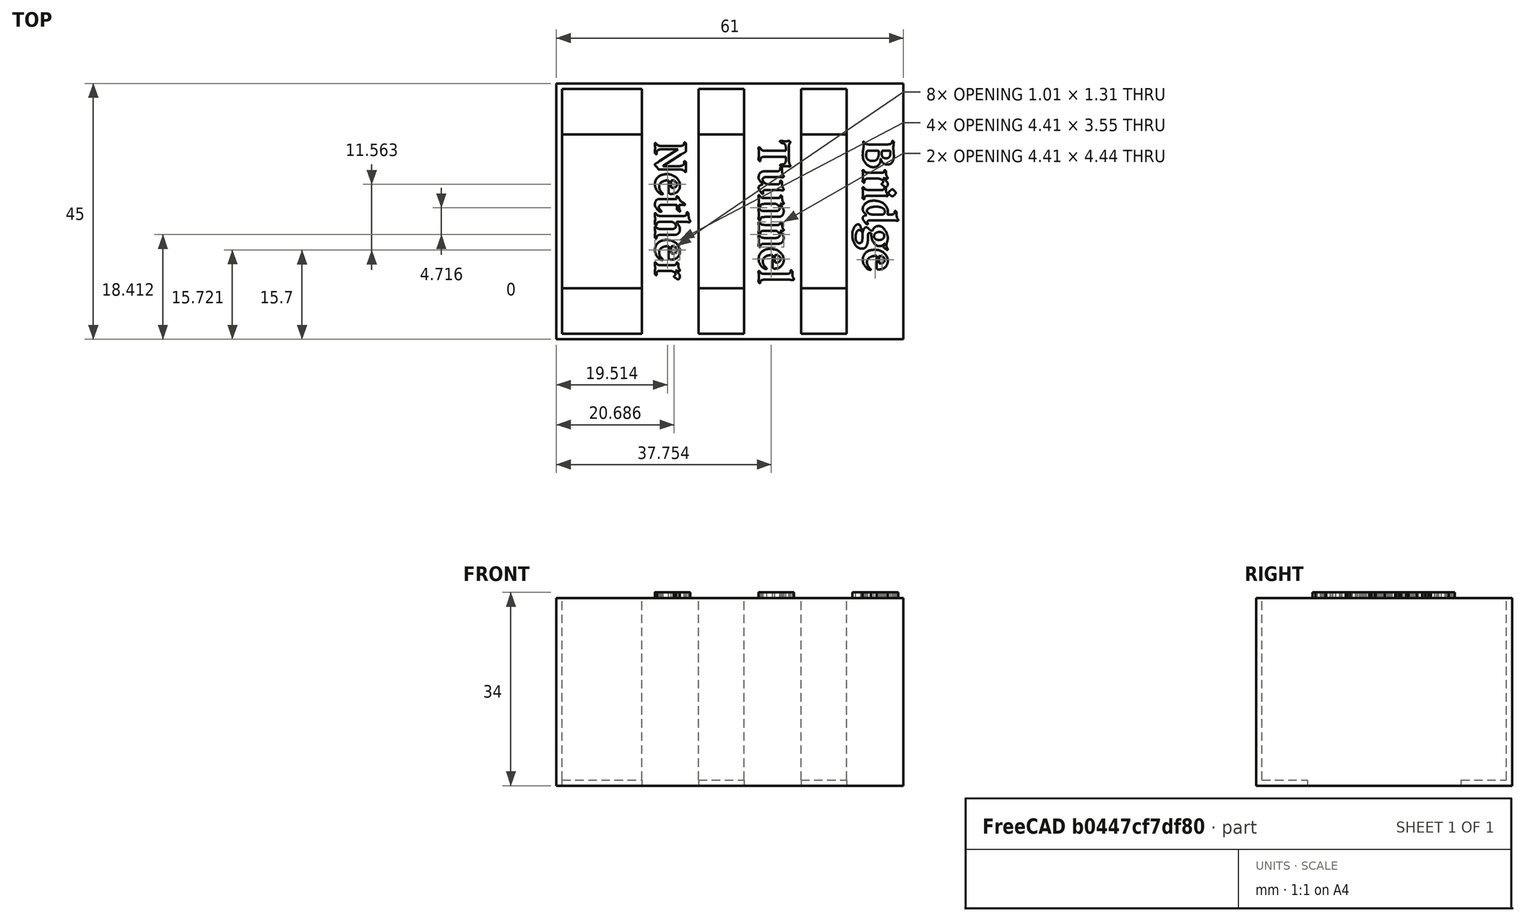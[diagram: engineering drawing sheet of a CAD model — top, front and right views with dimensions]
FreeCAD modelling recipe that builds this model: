
FCSTD DOCUMENT  (FreeCAD 0.18R4 (GitTag))
Label: lost_realms
License: All rights reserved
LicenseURL: http://en.wikipedia.org/wiki/All_rights_reserved
objects: Part::FeaturePython×21, Part::Box×9, Part::MultiFuse×7, Part::Extrusion×5, Part::Part2DObjectPython×3, Part::Cut×2, Part::Feature×1, Part::Plane×1, App::DocumentObjectGroup×1
note: 49 computed .brp shape members not serialized (recipe doc carries the construction recipe); baked Part::Feature solids carry a one-line shape summary decoded from their .brp

FEATURE [Part::Box] Box  label="Cube"
  AttacherType = Attacher::AttachEngine3D
  Height = 33
  Length = 202
  Placement = pos=(0,-1,0) rot=(0,0,1;0rad)
  Width = 45
FEATURE [Part::Box] Box001  label="Cube001"
  AttacherType = Attacher::AttachEngine3D
  Height = 33
  Length = 200
  Placement = pos=(1,0,0) rot=(0,0,1;0rad)
  Width = 43
FEATURE [Part::Cut] Cut
  Base = -> Box
  Tool = -> Box001
FEATURE [Part::Box] Box002  label="Cube002"
  AttacherType = Attacher::AttachEngine3D
  Height = 1
  Length = 202
  Width = 8
FEATURE [Part::Box] Box003  label="Cube003"
  AttacherType = Attacher::AttachEngine3D
  Height = 1
  Length = 202
  Placement = pos=(0,35,0) rot=(0,0,1;0rad)
  Width = 8
FEATURE [Part::MultiFuse] Fusion
  Shapes = -> [Cut,Box002,Box003]
FEATURE [Part::Box] Box004  label="Cube004"
  AttacherType = Attacher::AttachEngine3D
  Height = 33
  Length = 10
  Placement = pos=(15,0,0) rot=(0,0,1;0rad)
  Width = 43
FEATURE [Part::Box] Box005  label="Cube005"
  AttacherType = Attacher::AttachEngine3D
  Height = 33
  Length = 10
  Placement = pos=(33,0,0) rot=(0,0,1;0rad)
  Width = 43
FEATURE [Part::Box] Box006  label="Cube006"
  AttacherType = Attacher::AttachEngine3D
  Height = 33
  Length = 10
  Placement = pos=(51,0,0) rot=(0,0,1;0rad)
  Width = 43
FEATURE [Part::Box] Box007  label="Cube007"
  AttacherType = Attacher::AttachEngine3D
  Height = 33
  Length = 150
  Placement = pos=(61,-1,0) rot=(0,0,1;0rad)
  Width = 45
FEATURE [Part::MultiFuse] Fusion001
  Shapes = -> [Fusion,Box005,Box004,Box006]
FEATURE [Part::Cut] Cut001
  Base = -> Fusion001
  Tool = -> Box007
FEATURE [Part::Box] Box008  label="Cube008"
  AttacherType = Attacher::AttachEngine3D
  Height = 33
  Length = 10
  Placement = pos=(51,0,0) rot=(0,0,1;0rad)
  Width = 43
FEATURE [Part::MultiFuse] Fusion002
  Shapes = -> [Cut001,Box008]
FEATURE [Part::Part2DObjectPython] ShapeString  # Draft 2D object (typed FeaturePython)
  FontFile = <userpath>/Downloads/talisman/Caxton Bold.otf
  Size = 3
  String = Bridge
  Tracking = 0
FEATURE [Part::Extrusion] Extrude
  Base = -> ShapeString
  Dir = (0,0,1)
  DirMode = 2
  FaceMakerClass = Part::FaceMakerBullseye
  LengthFwd = 1
  LengthRev = 0
  Solid = false
  Symmetric = false
FEATURE [Part::Extrusion] Extrude001
  Base = -> ShapeString
  Dir = (0,0,1)
  DirMode = 2
  FaceMakerClass = Part::FaceMakerBullseye
  LengthFwd = 1
  LengthRev = 0
  Solid = false
  Symmetric = false
FEATURE [Part::Part2DObjectPython] ShapeString001  # Draft 2D object (typed FeaturePython)
  FontFile = <userpath>/Downloads/talisman/Caxton Bold.otf
  Placement = pos=(33,40.7,33) rot=(0,0,1;0rad)
  Size = 3
  String = Tunnel
  Tracking = 0
FEATURE [Part::Extrusion] Extrude002
  Base = -> ShapeString001
  Dir = (0,0,1)
  DirMode = 2
  FaceMakerClass = Part::FaceMakerBullseye
  LengthFwd = 1
  LengthRev = 0
  Placement = pos=(-5,67,0) rot=(0,0,-1;1.5708rad)
  Solid = false
  Symmetric = false
FEATURE [Part::Part2DObjectPython] ShapeString002  # Draft 2D object (typed FeaturePython)
  FontFile = <userpath>/Downloads/talisman/Caxton Bold.otf
  Placement = pos=(16.76,32.46,33) rot=(0,0,1;0rad)
  Size = 3
  String = Nether
  Tracking = 0
FEATURE [Part::Extrusion] Extrude003
  Base = -> ShapeString002
  Dir = (0,0,1)
  DirMode = 2
  FaceMakerClass = Part::FaceMakerBullseye
  LengthFwd = 1
  LengthRev = 0
  Solid = false
  Symmetric = false
FEATURE [Part::Extrusion] Extrude004
  Base = -> ShapeString002
  Dir = (0,0,1)
  DirMode = 2
  FaceMakerClass = Part::FaceMakerBullseye
  LengthFwd = 1
  LengthRev = 0
  Solid = false
  Symmetric = false
FEATURE [Part::MultiFuse] Fusion004
  Placement = pos=(-15,50.5,0) rot=(0,0,-1;1.5708rad)
  Shapes = -> [Extrude003,Extrude004]
FEATURE [Part::MultiFuse] Fusion006
  Placement = pos=(54,34,33) rot=(0,0,-1;1.5708rad)
  Shapes = -> [Extrude001,Extrude]
FEATURE [Part::MultiFuse] Fusion007
  Shapes = -> [Fusion006,Fusion002,Fusion004,Extrude002]
FEATURE [Part::Feature] Fusion007001  label="Fusion008"
  shape: bbox 61 x 45 x 34 mm, 504 faces (baked)
FEATURE [Part::Plane] Plane
  AttacherType = Attacher::AttachEngine3D
  Length = 200
  Placement = pos=(0,0,33) rot=(0,0,1;0rad)
  Width = 200
FEATURE [Part::FeaturePython] Slice  # WARN: FeaturePython — macro-defined, semantics opaque (R4)
  Base = -> Fusion007001
  Mode = 1
  Tolerance = 0
  Tools = -> [Plane]
FEATURE [Part::FeaturePython] Slice_child0  label="Slice.0"  # WARN: FeaturePython — macro-defined, semantics opaque (R4)
  Base = -> Slice
  FilterType = 1
  Invert = false
  OverrideMaxVal = 0
  WindowFrom = 80
  WindowTo = 100
  items = 0
FEATURE [Part::FeaturePython] Slice_child1  label="Slice.1"  # WARN: FeaturePython — macro-defined, semantics opaque (R4)
  Base = -> Slice
  FilterType = 1
  Invert = false
  OverrideMaxVal = 0
  WindowFrom = 80
  WindowTo = 100
  items = 1
FEATURE [Part::FeaturePython] Slice_child2  label="Slice.2"  # WARN: FeaturePython — macro-defined, semantics opaque (R4)
  Base = -> Slice
  FilterType = 1
  Invert = false
  OverrideMaxVal = 0
  WindowFrom = 80
  WindowTo = 100
  items = 2
FEATURE [Part::FeaturePython] Slice_child3  label="Slice.3"  # WARN: FeaturePython — macro-defined, semantics opaque (R4)
  Base = -> Slice
  FilterType = 1
  Invert = false
  OverrideMaxVal = 0
  WindowFrom = 80
  WindowTo = 100
  items = 3
FEATURE [Part::FeaturePython] Slice_child4  label="Slice.4"  # WARN: FeaturePython — macro-defined, semantics opaque (R4)
  Base = -> Slice
  FilterType = 1
  Invert = false
  OverrideMaxVal = 0
  WindowFrom = 80
  WindowTo = 100
  items = 4
FEATURE [Part::FeaturePython] Slice_child5  label="Slice.5"  # WARN: FeaturePython — macro-defined, semantics opaque (R4)
  Base = -> Slice
  FilterType = 1
  Invert = false
  OverrideMaxVal = 0
  WindowFrom = 80
  WindowTo = 100
  items = 5
FEATURE [Part::FeaturePython] Slice_child6  label="Slice.6"  # WARN: FeaturePython — macro-defined, semantics opaque (R4)
  Base = -> Slice
  FilterType = 1
  Invert = false
  OverrideMaxVal = 0
  WindowFrom = 80
  WindowTo = 100
  items = 6
FEATURE [Part::FeaturePython] Slice_child7  label="Slice.7"  # WARN: FeaturePython — macro-defined, semantics opaque (R4)
  Base = -> Slice
  FilterType = 1
  Invert = false
  OverrideMaxVal = 0
  WindowFrom = 80
  WindowTo = 100
  items = 7
FEATURE [Part::FeaturePython] Slice_child8  label="Slice.8"  # WARN: FeaturePython — macro-defined, semantics opaque (R4)
  Base = -> Slice
  FilterType = 1
  Invert = false
  OverrideMaxVal = 0
  WindowFrom = 80
  WindowTo = 100
  items = 8
FEATURE [Part::FeaturePython] Slice_child9  label="Slice.9"  # WARN: FeaturePython — macro-defined, semantics opaque (R4)
  Base = -> Slice
  FilterType = 1
  Invert = false
  OverrideMaxVal = 0
  WindowFrom = 80
  WindowTo = 100
  items = 9
FEATURE [Part::FeaturePython] Slice_child10  label="Slice.10"  # WARN: FeaturePython — macro-defined, semantics opaque (R4)
  Base = -> Slice
  FilterType = 1
  Invert = false
  OverrideMaxVal = 0
  WindowFrom = 80
  WindowTo = 100
  items = 10
FEATURE [Part::FeaturePython] Slice_child11  label="Slice.11"  # WARN: FeaturePython — macro-defined, semantics opaque (R4)
  Base = -> Slice
  FilterType = 1
  Invert = false
  OverrideMaxVal = 0
  WindowFrom = 80
  WindowTo = 100
  items = 11
FEATURE [Part::FeaturePython] Slice_child12  label="Slice.12"  # WARN: FeaturePython — macro-defined, semantics opaque (R4)
  Base = -> Slice
  FilterType = 1
  Invert = false
  OverrideMaxVal = 0
  WindowFrom = 80
  WindowTo = 100
  items = 12
FEATURE [Part::FeaturePython] Slice_child13  label="Slice.13"  # WARN: FeaturePython — macro-defined, semantics opaque (R4)
  Base = -> Slice
  FilterType = 1
  Invert = false
  OverrideMaxVal = 0
  WindowFrom = 80
  WindowTo = 100
  items = 13
FEATURE [Part::FeaturePython] Slice_child14  label="Slice.14"  # WARN: FeaturePython — macro-defined, semantics opaque (R4)
  Base = -> Slice
  FilterType = 1
  Invert = false
  OverrideMaxVal = 0
  WindowFrom = 80
  WindowTo = 100
  items = 14
FEATURE [Part::FeaturePython] Slice_child15  label="Slice.15"  # WARN: FeaturePython — macro-defined, semantics opaque (R4)
  Base = -> Slice
  FilterType = 1
  Invert = false
  OverrideMaxVal = 0
  WindowFrom = 80
  WindowTo = 100
  items = 15
FEATURE [Part::FeaturePython] Slice_child16  label="Slice.16"  # WARN: FeaturePython — macro-defined, semantics opaque (R4)
  Base = -> Slice
  FilterType = 1
  Invert = false
  OverrideMaxVal = 0
  WindowFrom = 80
  WindowTo = 100
  items = 16
FEATURE [Part::FeaturePython] Slice_child17  label="Slice.17"  # WARN: FeaturePython — macro-defined, semantics opaque (R4)
  Base = -> Slice
  FilterType = 1
  Invert = false
  OverrideMaxVal = 0
  WindowFrom = 80
  WindowTo = 100
  items = 17
FEATURE [Part::FeaturePython] Slice_child18  label="Slice.18"  # WARN: FeaturePython — macro-defined, semantics opaque (R4)
  Base = -> Slice
  FilterType = 1
  Invert = false
  OverrideMaxVal = 0
  WindowFrom = 80
  WindowTo = 100
  items = 18
FEATURE [Part::FeaturePython] Slice_child19  label="Slice.19"  # WARN: FeaturePython — macro-defined, semantics opaque (R4)
  Base = -> Slice
  FilterType = 1
  Invert = false
  OverrideMaxVal = 0
  WindowFrom = 80
  WindowTo = 100
  items = 19
FEATURE [Part::MultiFuse] Fusion007002
  Shapes = -> [Slice_child1,Slice_child6,Slice_child11,Slice_child4,Slice_child18,Slice_child19,Slice_child16,Slice_child12,Slice_child8,Slice_child9,Slice_child14,Slice_child13,Slice_child2,Slice_child3,Slice_child10,Slice_child7,Slice_child5,Slice_child15,Slice_child17]
FEATURE [App::DocumentObjectGroup] GrExplode_Slice  label="Exploded Slice"
  Group = -> [Slice_child0,Fusion007002]
